# Revit family: Power-MouldedCaseDevices-GEWISS-97MSS-SWITCH_DISCONNECTOR_125
name_source: partatom
category: Apparecchi elettrici
revit_build: Autodesk Revit 2016 (Build: 20161004_0715(x64)
units: mm (PartAtom-declared; Revit-internal decimal feet)

## family parameters
Condiviso = No
Host = Muro
Mantenere orientamento annotazione = Sì
Numero OmniClass = 23.80.30.00
Punto di calcolo locali = Sì
Quota connettore circolare = Usa diametro
Sempre verticale = Sì
Taglio con vuoti quando caricato = No
Tipo di parte = Normale
Titolo OmniClass = Distribution Devices

## types (6) — shared parameters
Catalogue = POWER
Catalogue Range = 97 MSS
GW - Codice Electrocod = 150
IDF = 0625bfaf-6454-4439-8049-c923d73cca22
IDT = bc1ed70b-553e-473f-adfe-2a6bdbceff6d
Immagine tipo = GW97726.jpg
Label = MSS 125
No. Chorus modules = 6
No. of modules EN 50022 = 6
Produttore = GEWISS S.p.A.
Rated voltage = 400V
SEO = Disconnector
Technical sheet = https://www.gewiss.com
URL = https://www.gewiss.com
Version file RFA = 18.0

## per-type parameters (varying)
| type | Descrizione | EAN code | Modello | No. of poles | Number of poles | Rated current (In) | Rated current: |
| GW97723 - SWITCH DISCONNECTOR MSS 125 3P 125A | SWITCH DISCONNECTOR MSS 125 3P 125A | 8011564211438 | GW97723 | 3P | 3P | 125A | 125A |
| GW97722 - SWITCH DISCONNECTOR MSS 125 3P 100A | SWITCH DISCONNECTOR MSS 125 3P 100A | 8011564211421 | GW97722 | 3P | 3P | 100A | 100A |
| GW97721 - SWITCH DISCONNECTOR MSS 125 3P 63A | SWITCH DISCONNECTOR MSS 125 3P 63A | 8011564211414 | GW97721 | 3P | 3P | 63A | 63A |
| GW97725 - SWITCH DISCONNECTOR MSS 125 4P 100A | SWITCH DISCONNECTOR MSS 125 4P 100A | 8011564211452 | GW97725 | 4P | 4P | 100A | 100A |
| GW97726 - SWITCH DISCONNECTOR MSS 125 4P 125A | SWITCH DISCONNECTOR MSS 125 4P 125A | 8011564211469 | GW97726 | 4P | 4P | 125A | 125A |
| GW97724 - SWITCH DISCONNECTOR MSS 125 4P 63A | SWITCH DISCONNECTOR MSS 125 4P 63A | 8011564211445 | GW97724 | 4P | 4P | 63A | 63A |
